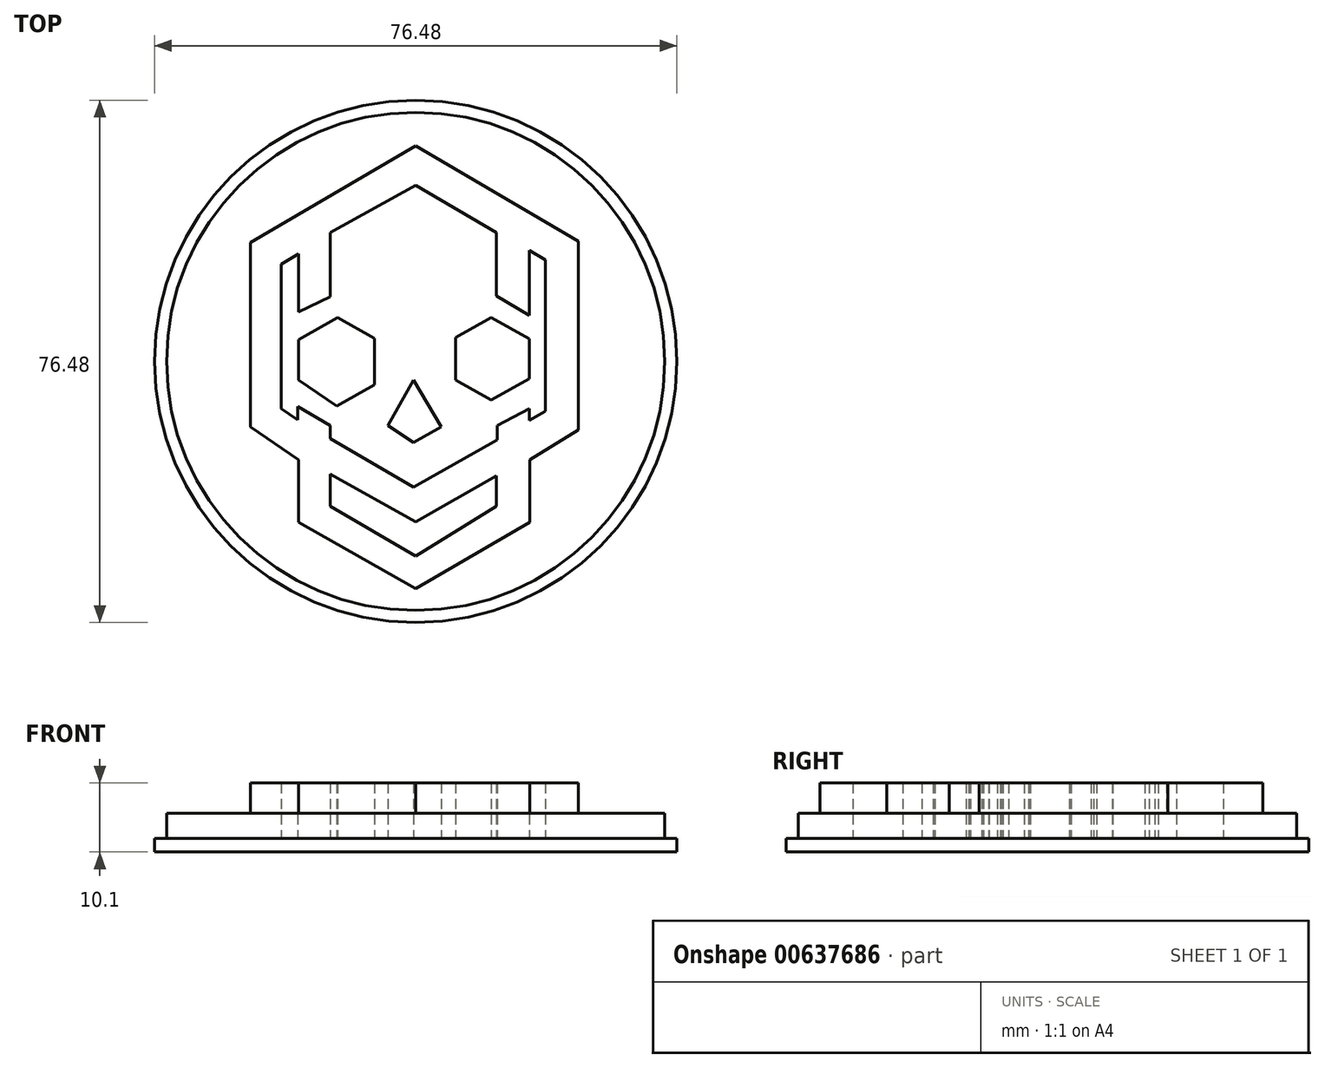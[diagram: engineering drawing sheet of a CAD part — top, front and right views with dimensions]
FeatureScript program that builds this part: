
annotation { "Feature Type Name" : "Feature", "Feature Type Description" : "" }
export const myFeature = defineFeature(function(context is Context, id is Id, definition is map)
    precondition{}
    {
        {
            var Q0;
            Q0=qCreatedBy(makeId("Top.planeOp"),FACE);
            var sketch = newSketch(context, id + "F0", { "sketchPlane" : qUnion([Q0])});
            skCircle(sketch, "E0", {"center": v(0, 0) * mm, "radius": 36.48 * mm});
            skLineSegment(sketch, "E1", {"start": v(0, 31.54) * mm, "end": v(-24.21, 17.41) * mm});
            skLineSegment(sketch, "E2", {"start": v(-24.21, 17.41) * mm, "end": v(-24.21, -9.6) * mm});
            skLineSegment(sketch, "E3", {"start": v(-24.21, -9.6) * mm, "end": v(-17.15, -14.38) * mm});
            skLineSegment(sketch, "E4", {"start": v(-17.15, -14.38) * mm, "end": v(-17.15, -23.53) * mm});
            skLineSegment(sketch, "E5", {"start": v(-17.15, -23.53) * mm, "end": v(0, -33.3) * mm});
            skLineSegment(sketch, "E6", {"start": v(0, -33.3) * mm, "end": v(16.73, -23.53) * mm});
            skLineSegment(sketch, "E7", {"start": v(16.73, -23.53) * mm, "end": v(16.73, -14.38) * mm});
            skLineSegment(sketch, "E8", {"start": v(16.73, -14.38) * mm, "end": v(23.8, -10.02) * mm});
            skLineSegment(sketch, "E9", {"start": v(23.8, -10.02) * mm, "end": v(23.8, 17.62) * mm});
            skLineSegment(sketch, "E10", {"start": v(23.8, 17.62) * mm, "end": v(0, 31.54) * mm});
            skLineSegment(sketch, "E11", {"start": v(-17.15, 7.23) * mm, "end": v(-17.15, 15.75) * mm});
            skLineSegment(sketch, "E12", {"start": v(-17.15, 15.75) * mm, "end": v(-19.7, 14.26) * mm});
            skLineSegment(sketch, "E13", {"start": v(-19.7, 14.26) * mm, "end": v(-19.7, -6.9) * mm});
            skLineSegment(sketch, "E14", {"start": v(-19.7, -6.9) * mm, "end": v(-17.28, -8.54) * mm});
            skLineSegment(sketch, "E15", {"start": v(-17.28, -8.54) * mm, "end": v(-17.28, -6.6) * mm});
            skLineSegment(sketch, "E16", {"start": v(-17.28, -6.6) * mm, "end": v(-12.53, -9.37) * mm});
            skLineSegment(sketch, "E17", {"start": v(-12.53, -9.37) * mm, "end": v(-12.53, -11.3) * mm});
            skLineSegment(sketch, "E18", {"start": v(-12.53, -11.3) * mm, "end": v(-0.35, -18.4) * mm});
            skLineSegment(sketch, "E19", {"start": v(-0.35, -18.4) * mm, "end": v(11.95, -11.51) * mm});
            skLineSegment(sketch, "E20", {"start": v(11.95, -11.51) * mm, "end": v(11.95, -9.37) * mm});
            skLineSegment(sketch, "E21", {"start": v(11.95, -9.37) * mm, "end": v(16.63, -6.9) * mm});
            skLineSegment(sketch, "E22", {"start": v(16.63, -6.9) * mm, "end": v(16.63, -8.6) * mm});
            skLineSegment(sketch, "E23", {"start": v(16.63, -8.6) * mm, "end": v(18.99, -7.3) * mm});
            skLineSegment(sketch, "E24", {"start": v(18.99, -7.3) * mm, "end": v(18.99, 14.87) * mm});
            skLineSegment(sketch, "E25", {"start": v(18.99, 14.87) * mm, "end": v(16.63, 16.24) * mm});
            skLineSegment(sketch, "E26", {"start": v(16.63, 16.24) * mm, "end": v(16.63, 6.75) * mm});
            skLineSegment(sketch, "E27", {"start": v(16.63, 6.75) * mm, "end": v(11.82, 9.56) * mm});
            skLineSegment(sketch, "E28", {"start": v(11.82, 9.56) * mm, "end": v(11.82, 18.89) * mm});
            skLineSegment(sketch, "E29", {"start": v(11.82, 18.89) * mm, "end": v(0, 25.78) * mm});
            skLineSegment(sketch, "E30", {"start": v(0, 25.78) * mm, "end": v(-12.53, 18.89) * mm});
            skLineSegment(sketch, "E31", {"start": v(-12.53, 18.89) * mm, "end": v(-12.53, 9.48) * mm});
            skLineSegment(sketch, "E32", {"start": v(-12.53, 9.48) * mm, "end": v(-17.15, 7.23) * mm});
            skLineSegment(sketch, "E33", {"start": v(-12.53, -16.48) * mm, "end": v(-12.53, -21.18) * mm});
            skLineSegment(sketch, "E34", {"start": v(-12.53, -21.18) * mm, "end": v(0, -28.48) * mm});
            skLineSegment(sketch, "E35", {"start": v(0, -28.48) * mm, "end": v(11.82, -21.18) * mm});
            skLineSegment(sketch, "E36", {"start": v(11.82, -21.18) * mm, "end": v(11.82, -16.73) * mm});
            skLineSegment(sketch, "E37", {"start": v(11.82, -16.73) * mm, "end": v(0, -23.52) * mm});
            skLineSegment(sketch, "E38", {"start": v(0, -23.52) * mm, "end": v(-12.53, -16.48) * mm});
            skLineSegment(sketch, "E39", {"start": v(-0.35, -2.74) * mm, "end": v(-4.07, -9.37) * mm});
            skLineSegment(sketch, "E40", {"start": v(-4.07, -9.37) * mm, "end": v(-0.35, -11.9) * mm});
            skLineSegment(sketch, "E41", {"start": v(-0.35, -11.9) * mm, "end": v(3.75, -9.6) * mm});
            skLineSegment(sketch, "E42", {"start": v(3.75, -9.6) * mm, "end": v(-0.35, -2.74) * mm});
            skLineSegment(sketch, "E43", {"start": v(-11.42, 6.4) * mm, "end": v(-17.15, 3.18) * mm});
            skLineSegment(sketch, "E44", {"start": v(-17.15, 3.18) * mm, "end": v(-17.15, -2.74) * mm});
            skLineSegment(sketch, "E45", {"start": v(-17.15, -2.74) * mm, "end": v(-11.56, -6.52) * mm});
            skLineSegment(sketch, "E46", {"start": v(-11.56, -6.52) * mm, "end": v(-6.04, -3.42) * mm});
            skLineSegment(sketch, "E47", {"start": v(-6.04, -3.42) * mm, "end": v(-6.04, 3.38) * mm});
            skLineSegment(sketch, "E48", {"start": v(-6.04, 3.38) * mm, "end": v(-11.42, 6.4) * mm});
            skLineSegment(sketch, "E49", {"start": v(11.04, 6.4) * mm, "end": v(5.84, 3.48) * mm});
            skLineSegment(sketch, "E50", {"start": v(5.84, 3.48) * mm, "end": v(5.84, -2.74) * mm});
            skLineSegment(sketch, "E51", {"start": v(5.84, -2.74) * mm, "end": v(11.03, -5.66) * mm});
            skLineSegment(sketch, "E52", {"start": v(11.03, -5.66) * mm, "end": v(16.63, -2.52) * mm});
            skLineSegment(sketch, "E53", {"start": v(16.63, -2.52) * mm, "end": v(16.63, 3.3) * mm});
            skLineSegment(sketch, "E54", {"start": v(16.63, 3.3) * mm, "end": v(11.04, 6.4) * mm});
            skSolve(sketch);
        }
        {
            var Q0;
            Q0 = qSketchRegion(id + "F0", true);
            var Q1;
            Q1=makeQuery(id+"F0.imprint","IMPRINT",FACE,{"disambiguationData":[TD([[makeQuery(id+"F0.imprint","IMPRINT",EDGE,{"derivedFrom":sQuery(id+"F0.wireOp",EDGE,"E0")}),1.0]])]});
            extrude(context, id + "F1", {"entities" : qUnion([Q0, Q1]), "depth" : 3.7 * mm, "offsetDistance" : 25 * mm});
        }
        {
            var Q0;
            Q0=makeQuery(id+"F0.imprint","IMPRINT",FACE,{"disambiguationData":[TD([[makeQuery(id+"F0.imprint","IMPRINT",EDGE,{"derivedFrom":sQuery(id+"F0.wireOp",EDGE,"E1")}),1.0]])]});
            var Q1;
            Q1=makeQuery(id+"F0.imprint","IMPRINT",FACE,{"disambiguationData":[TD([[makeQuery(id+"F0.imprint","IMPRINT",EDGE,{"derivedFrom":sQuery(id+"F0.wireOp",EDGE,"E49")}),1.0]])]});
            var Q2;
            Q2=makeQuery(id+"F0.imprint","IMPRINT",FACE,{"disambiguationData":[TD([[makeQuery(id+"F0.imprint","IMPRINT",EDGE,{"derivedFrom":sQuery(id+"F0.wireOp",EDGE,"E43")}),1.0]])]});
            var Q3;
            Q3=makeQuery(id+"F0.imprint","IMPRINT",FACE,{"disambiguationData":[TD([[makeQuery(id+"F0.imprint","IMPRINT",EDGE,{"derivedFrom":sQuery(id+"F0.wireOp",EDGE,"E39")}),1.0]])]});
            extrude(context, id + "F2", {"entities" : qUnion([Q0, Q1, Q2, Q3]), "operationType" : NewBodyOperationType.ADD, "depth" : 8.1 * mm, "offsetDistance" : 25 * mm});
        }
        {
            var Q0;
            Q0=qCreatedBy(makeId("Top.planeOp"),FACE);
            var sketch = newSketch(context, id + "F3", { "sketchPlane" : qUnion([Q0])});
            skCircle(sketch, "E55", {"center": v(0, 0) * mm, "radius": 38.24 * mm});
            skSolve(sketch);
        }
        {
            var Q0;
            Q0=makeQuery(id+"F3.imprint","IMPRINT",FACE,{"disambiguationData":[TD([[makeQuery(id+"F3.imprint","IMPRINT",EDGE,{"derivedFrom":sQuery(id+"F3.wireOp",EDGE,"E55")}),1.0]])]});
            extrude(context, id + "F4", {"entities" : qUnion([Q0]), "operationType" : NewBodyOperationType.ADD, "oppositeDirection" : true, "depth" : 2 * mm, "offsetDistance" : 25 * mm});
        }
    });
